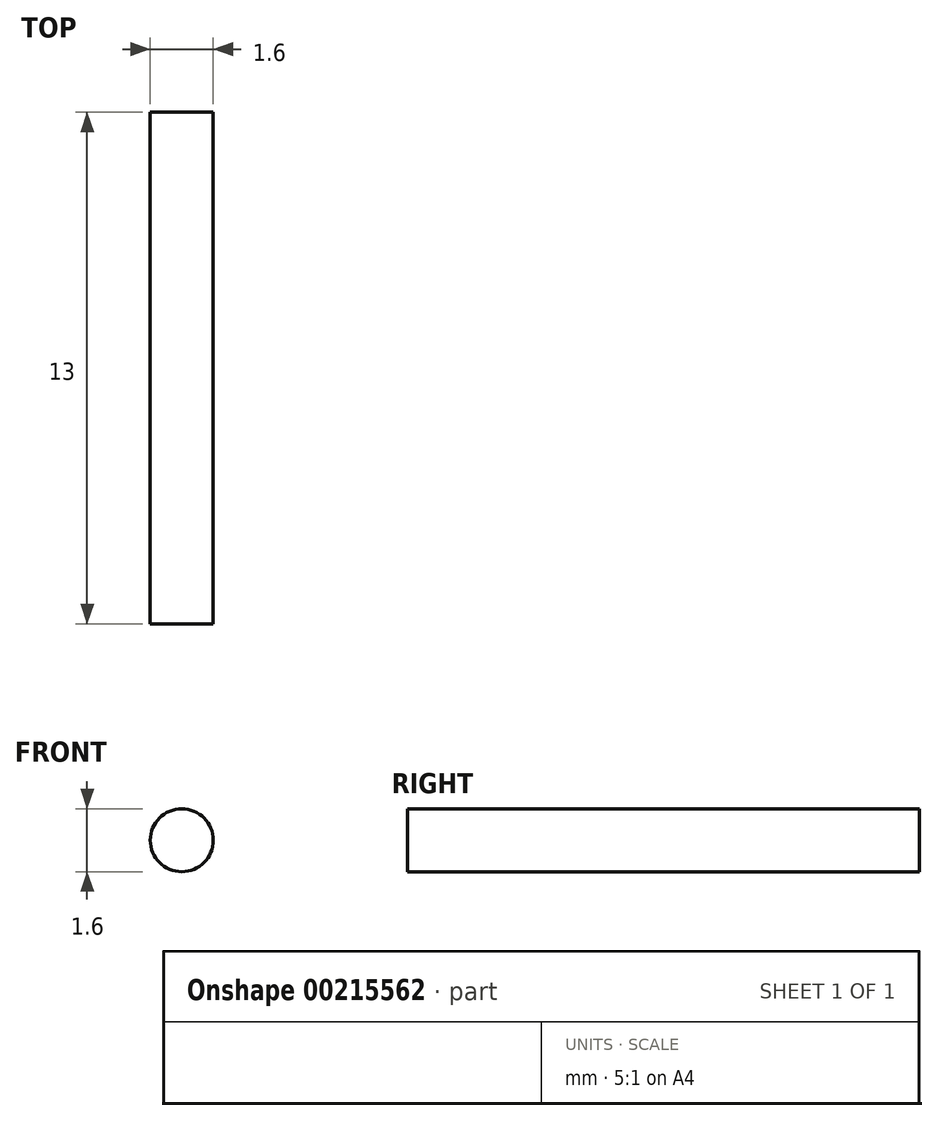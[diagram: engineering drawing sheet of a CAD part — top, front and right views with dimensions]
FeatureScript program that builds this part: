
annotation { "Feature Type Name" : "Feature", "Feature Type Description" : "" }
export const myFeature = defineFeature(function(context is Context, id is Id, definition is map)
    precondition{}
    {
        {
            var Q0;
            Q0=qCreatedBy(makeId("Front.planeOp"),FACE);
            var sketch = newSketch(context, id + "F0", { "sketchPlane" : qUnion([Q0])});
            skCircle(sketch, "E0", {"center": v(0, 0) * mm, "radius": 0.8 * mm});
            skSolve(sketch);
        }
        {
            var Q0;
            Q0 = qSketchRegion(id + "F0", true);
            extrude(context, id + "F1", {"entities" : qUnion([Q0]), "depth" : 13 * mm});
        }
    });
